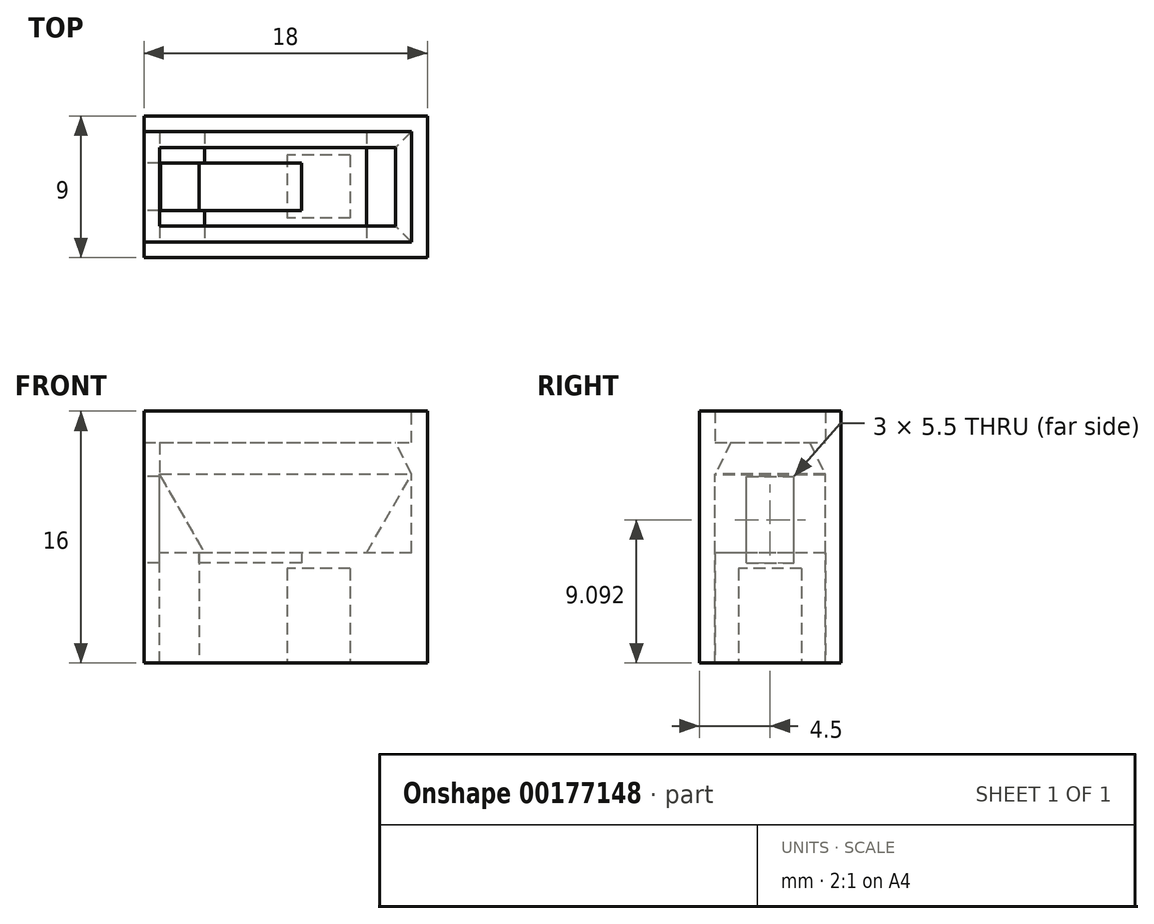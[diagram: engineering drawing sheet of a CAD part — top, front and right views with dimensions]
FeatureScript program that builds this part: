
annotation { "Feature Type Name" : "Feature", "Feature Type Description" : "" }
export const myFeature = defineFeature(function(context is Context, id is Id, definition is map)
    precondition{}
    {
        {
            var Q0;
            Q0=qCreatedBy(makeId("Top.planeOp"),FACE);
            var sketch = newSketch(context, id + "F0", { "sketchPlane" : qUnion([Q0])});
            skLineSegment(sketch, "E0.bottom", {"start": v(9, -4.5) * mm, "end": v(-9, -4.5) * mm});
            skLineSegment(sketch, "E0.top", {"start": v(9, 4.5) * mm, "end": v(-9, 4.5) * mm});
            skLineSegment(sketch, "E0.left", {"start": v(9, -4.5) * mm, "end": v(9, 4.5) * mm});
            skLineSegment(sketch, "E0.right", {"start": v(-9, -4.5) * mm, "end": v(-9, 4.5) * mm});
            skPoint(sketch, "E0.middle", {"position": v(0, 0) * mm});
            skSolve(sketch);
        }
        {
            var Q0;
            Q0=qSketchRegion(id+"F0",true);
            extrude(context, id + "F1", {"entities" : qUnion([Q0]), "depth" : 14 * mm});
        }
        {
            var Q0;
            Q0=makeQuery(id+"F1.opExtrude","CAP_FACE",FACE,{"disambiguationData":[OSD([sQuery(id+"F0.wireOp",EDGE,"E0.bottom"),sQuery(id+"F0.wireOp",EDGE,"E0.top"),sQuery(id+"F0.wireOp",EDGE,"E0.left"),sQuery(id+"F0.wireOp",EDGE,"E0.right")])],"isStart":false});
            var sketch = newSketch(context, id + "F2", { "sketchPlane" : qUnion([Q0])});
            skLineSegment(sketch, "E1.bottom", {"start": v(8, -3.5) * mm, "end": v(-8, -3.5) * mm});
            skLineSegment(sketch, "E1.top", {"start": v(8, 3.5) * mm, "end": v(-8, 3.5) * mm});
            skLineSegment(sketch, "E1.left", {"start": v(8, -3.5) * mm, "end": v(8, 3.5) * mm});
            skLineSegment(sketch, "E1.right", {"start": v(-8, -3.5) * mm, "end": v(-8, 3.5) * mm});
            skPoint(sketch, "E1.middle", {"position": v(0, 0) * mm});
            skSolve(sketch);
        }
        {
            var Q0;
            Q0=qSketchRegion(id+"F2",true);
            extrude(context, id + "F3", {"entities" : qUnion([Q0]), "operationType" : NewBodyOperationType.REMOVE, "oppositeDirection" : true, "depth" : 7 * mm});
        }
        {
            var Q0;
            Q0=makeQuery(id+"F1.opExtrude","CAP_FACE",FACE,{"disambiguationData":[OSD([sQuery(id+"F0.wireOp",EDGE,"E0.bottom"),sQuery(id+"F0.wireOp",EDGE,"E0.top"),sQuery(id+"F0.wireOp",EDGE,"E0.left"),sQuery(id+"F0.wireOp",EDGE,"E0.right")])],"isStart":true});
            var sketch = newSketch(context, id + "F4", { "sketchPlane" : qUnion([Q0])});
            skLineSegment(sketch, "E2.bottom", {"start": v(4.1, -2) * mm, "end": v(0.1, -2) * mm});
            skLineSegment(sketch, "E2.top", {"start": v(4.1, 2) * mm, "end": v(0.1, 2) * mm});
            skLineSegment(sketch, "E2.left", {"start": v(4.1, -2) * mm, "end": v(4.1, 2) * mm});
            skLineSegment(sketch, "E2.right", {"start": v(0.1, -2) * mm, "end": v(0.1, 2) * mm});
            skPoint(sketch, "E2.middle", {"position": v(2.1, 0) * mm});
            skLineSegment(sketch, "E3.bottom", {"start": v(-5.5, -3.5) * mm, "end": v(-8, -3.5) * mm});
            skLineSegment(sketch, "E3.top", {"start": v(-5.5, 3.5) * mm, "end": v(-8, 3.5) * mm});
            skLineSegment(sketch, "E3.left", {"start": v(-5.5, -3.5) * mm, "end": v(-5.5, 3.5) * mm});
            skLineSegment(sketch, "E3.right", {"start": v(-8, -3.5) * mm, "end": v(-8, 3.5) * mm});
            skPoint(sketch, "E3.middle", {"position": v(-6.75, 0) * mm});
            skSolve(sketch);
        }
        {
            var Q0;
            Q0=makeQuery(id+"F4.imprint","IMPRINT",FACE,{"disambiguationData":[TD([[makeQuery(id+"F4.imprint","IMPRINT",EDGE,{"derivedFrom":sQuery(id+"F4.wireOp",EDGE,"E2.bottom")}),-1.0]])]});
            extrude(context, id + "F5", {"entities" : qUnion([Q0]), "operationType" : NewBodyOperationType.REMOVE, "oppositeDirection" : true, "depth" : 6 * mm});
        }
        {
            var Q0;
            Q0=makeQuery(id+"F4.imprint","IMPRINT",FACE,{"disambiguationData":[TD([[makeQuery(id+"F4.imprint","IMPRINT",EDGE,{"derivedFrom":sQuery(id+"F4.wireOp",EDGE,"E3.bottom")}),-1.0]])]});
            extrude(context, id + "F6", {"entities" : qUnion([Q0]), "operationType" : NewBodyOperationType.REMOVE, "oppositeDirection" : true, "depth" : 9 * mm});
        }
        {
            var Q0;
            Q0=makeQuery(id+"F1.opExtrude","CAP_FACE",FACE,{"disambiguationData":[OSD([sQuery(id+"F0.wireOp",EDGE,"E0.bottom"),sQuery(id+"F0.wireOp",EDGE,"E0.top"),sQuery(id+"F0.wireOp",EDGE,"E0.left"),sQuery(id+"F0.wireOp",EDGE,"E0.right")])],"isStart":false});
            var sketch = newSketch(context, id + "F7", { "sketchPlane" : qUnion([Q0])});
            skLineSegment(sketch, "E4", {"start": v(-9, 4.5) * mm, "end": v(9, 4.5) * mm});
            skLineSegment(sketch, "E5", {"start": v(9, 4.5) * mm, "end": v(9, -4.5) * mm});
            skLineSegment(sketch, "E6", {"start": v(9, -4.5) * mm, "end": v(-9, -4.5) * mm});
            skLineSegment(sketch, "E7", {"start": v(-9, -4.5) * mm, "end": v(-9, -3.5) * mm});
            skLineSegment(sketch, "E8", {"start": v(-9, -3.5) * mm, "end": v(8, -3.5) * mm});
            skLineSegment(sketch, "E9", {"start": v(8, -3.5) * mm, "end": v(8, 3.5) * mm});
            skLineSegment(sketch, "E10", {"start": v(8, 3.5) * mm, "end": v(-9, 3.5) * mm});
            skLineSegment(sketch, "E11", {"start": v(-9, 3.5) * mm, "end": v(-9, 4.5) * mm});
            skSolve(sketch);
        }
        {
            var Q0;
            Q0=qSketchRegion(id+"F7",true);
            extrude(context, id + "F8", {"entities" : qUnion([Q0]), "operationType" : NewBodyOperationType.ADD, "depth" : 2 * mm});
        }
        {
            var Q0;
            Q0=makeQuery(id+"F8.boolean.opBoolean","MERGE",FACE,{"derivedFrom":[makeQuery(id+"F6.boolean.opBoolean","MERGE",FACE,{"derivedFrom":[makeQuery(id+"F3.boolean.opBoolean","COPY",FACE,{"derivedFrom":makeQuery(id+"F3.opExtrude","SWEPT_FACE",FACE,{"disambiguationData":[OSD([sQuery(id+"F2.wireOp",EDGE,"E1.bottom")])]})}),makeQuery(id+"F6.opExtrude","SWEPT_FACE",FACE,{"disambiguationData":[OSD([sQuery(id+"F4.wireOp",EDGE,"E3.top")])]})]}),makeQuery(id+"F8.opExtrude","SWEPT_FACE",FACE,{"disambiguationData":[OSD([sQuery(id+"F7.wireOp",EDGE,"E8")])]})]});
            var sketch = newSketch(context, id + "F9", { "sketchPlane" : qUnion([Q0])});
            skLineSegment(sketch, "E12", {"start": v(-8, 14) * mm, "end": v(-7, 14) * mm});
            skLineSegment(sketch, "E13", {"start": v(-7, 14) * mm, "end": v(-8, 12) * mm});
            skLineSegment(sketch, "E14", {"start": v(-8, 12) * mm, "end": v(-8, 14) * mm});
            skLineSegment(sketch, "E15", {"start": v(-8, 7) * mm, "end": v(-5.14, 7) * mm});
            skLineSegment(sketch, "E16", {"start": v(-5.14, 7) * mm, "end": v(-8, 11.95) * mm});
            skLineSegment(sketch, "E17", {"start": v(-8, 11.95) * mm, "end": v(-8, 7) * mm});
            skLineSegment(sketch, "E18", {"start": v(8, 11.95) * mm, "end": v(5.14, 7) * mm});
            skLineSegment(sketch, "E19", {"start": v(5.14, 7) * mm, "end": v(8, 7) * mm});
            skLineSegment(sketch, "E20", {"start": v(8, 7) * mm, "end": v(8, 11.95) * mm});
            skSolve(sketch);
        }
        {
            var Q0;
            Q0=qSketchRegion(id+"F9",true);
            extrude(context, id + "F10", {"entities" : qUnion([Q0]), "depth" : 7 * mm});
        }
        {
            var Q0;
            Q0=makeQuery(id+"F8.boolean.opBoolean","MERGE",FACE,{"derivedFrom":[makeQuery(id+"F3.boolean.opBoolean","COPY",FACE,{"derivedFrom":makeQuery(id+"F3.opExtrude","SWEPT_FACE",FACE,{"disambiguationData":[OSD([sQuery(id+"F2.wireOp",EDGE,"E1.left")])]})}),makeQuery(id+"F8.opExtrude","SWEPT_FACE",FACE,{"disambiguationData":[OSD([sQuery(id+"F7.wireOp",EDGE,"E9")])]})]});
            var sketch = newSketch(context, id + "F11", { "sketchPlane" : qUnion([Q0])});
            skLineSegment(sketch, "E21", {"start": v(3.5, 14) * mm, "end": v(2.5, 14) * mm});
            skLineSegment(sketch, "E22", {"start": v(-2.5, 14) * mm, "end": v(-3.5, 14) * mm});
            skLineSegment(sketch, "E23", {"start": v(2.5, 14) * mm, "end": v(3.5, 12) * mm});
            skLineSegment(sketch, "E24", {"start": v(3.5, 12) * mm, "end": v(3.5, 14) * mm});
            skLineSegment(sketch, "E25", {"start": v(-2.5, 14) * mm, "end": v(-3.5, 12) * mm});
            skLineSegment(sketch, "E26", {"start": v(-3.5, 12) * mm, "end": v(-3.5, 14) * mm});
            skSolve(sketch);
        }
        {
            var Q0;
            Q0=qSketchRegion(id+"F11",true);
            extrude(context, id + "F12", {"entities" : qUnion([Q0]), "operationType" : NewBodyOperationType.ADD, "depth" : 16 * mm});
        }
        {
            var Q0;
            Q0=makeQuery(id+"F8.boolean.opBoolean","MERGE",FACE,{"derivedFrom":[makeQuery(id+"F1.opExtrude","SWEPT_FACE",FACE,{"disambiguationData":[OSD([sQuery(id+"F0.wireOp",EDGE,"E0.right")])]}),makeQuery(id+"F8.opExtrude","SWEPT_FACE",FACE,{"disambiguationData":[OSD([sQuery(id+"F7.wireOp",EDGE,"E7")])]}),makeQuery(id+"F8.opExtrude","SWEPT_FACE",FACE,{"disambiguationData":[OSD([sQuery(id+"F7.wireOp",EDGE,"E11")])]})]});
            var sketch = newSketch(context, id + "F13", { "sketchPlane" : qUnion([Q0])});
            skLineSegment(sketch, "E27.bottom", {"start": v(-1.5, 11.84) * mm, "end": v(1.5, 11.84) * mm});
            skLineSegment(sketch, "E27.top", {"start": v(-1.5, 6.34) * mm, "end": v(1.5, 6.34) * mm});
            skLineSegment(sketch, "E27.left", {"start": v(-1.5, 11.84) * mm, "end": v(-1.5, 6.34) * mm});
            skLineSegment(sketch, "E27.right", {"start": v(1.5, 11.84) * mm, "end": v(1.5, 6.34) * mm});
            skSolve(sketch);
        }
        {
            var Q0;
            Q0=qSketchRegion(id+"F13",true);
            extrude(context, id + "F14", {"entities" : qUnion([Q0]), "operationType" : NewBodyOperationType.REMOVE, "oppositeDirection" : true, "depth" : 10 * mm});
        }
    });
